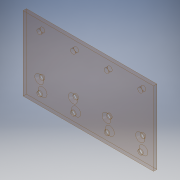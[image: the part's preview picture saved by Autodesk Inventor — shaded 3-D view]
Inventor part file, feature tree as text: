
AUTODESK INVENTOR PART (.ipt)
format: ipt  version: 2019 (Build 230136000, 136)  size: 144,896 bytes
history: native  units: in
note: dims shown in document units (in); Inventor stores cm internally (conversion verified against a paired STEP export)
features: sketch x4, hole x3, projected_geometry x2, extrude x1
ambient origin geometry x8: Origin, YZ Plane, XZ Plane, XY Plane, X Axis, Y Axis, Z Axis, Center Point
bodies: Solid1 (feature_tree)
feature tree (10):
  extrude  "Extrusion1"  Depth=4.85in
  hole  "Hole1"  [1 undecoded]
  hole  "Hole2"  [1 undecoded]
  hole  "Hole3"  [1 undecoded]
  sketch  "Sketch1"  dims[d0=2.75in d1=4.85in]
  sketch  "Sketch2"  dims[d2=0.125in d3=0.0in d5=0.385in]
  sketch  "Sketch3"  dims[d6=0.6in d7=1.25in]
  projected_geometry  "Projected Loop1"
  sketch  "Sketch4"  dims[d8=1.25in d9=1.25in d10=0.177in d11=0.75in d12=0.385in d13=0.25in d14=0.5635in d15=1.0in d16=0.8108in d19=0.177in d20=1.717in d21=0.332in d22=0.25in d23=0.5635in d24=1.0in d25=0.8108in d26=2.0in d27=0.177in d28=1.717in d29=0.332in d30=0.25in d31=0.5635in d32=1.0in d33=0.8108in]
  projected_geometry  "Projected Loop2"
note: 3 required parameter values undecoded (feature->parameter linkage not recoverable at this tier; creation-order binding heuristic only, values carry confidence <= 0.55)
